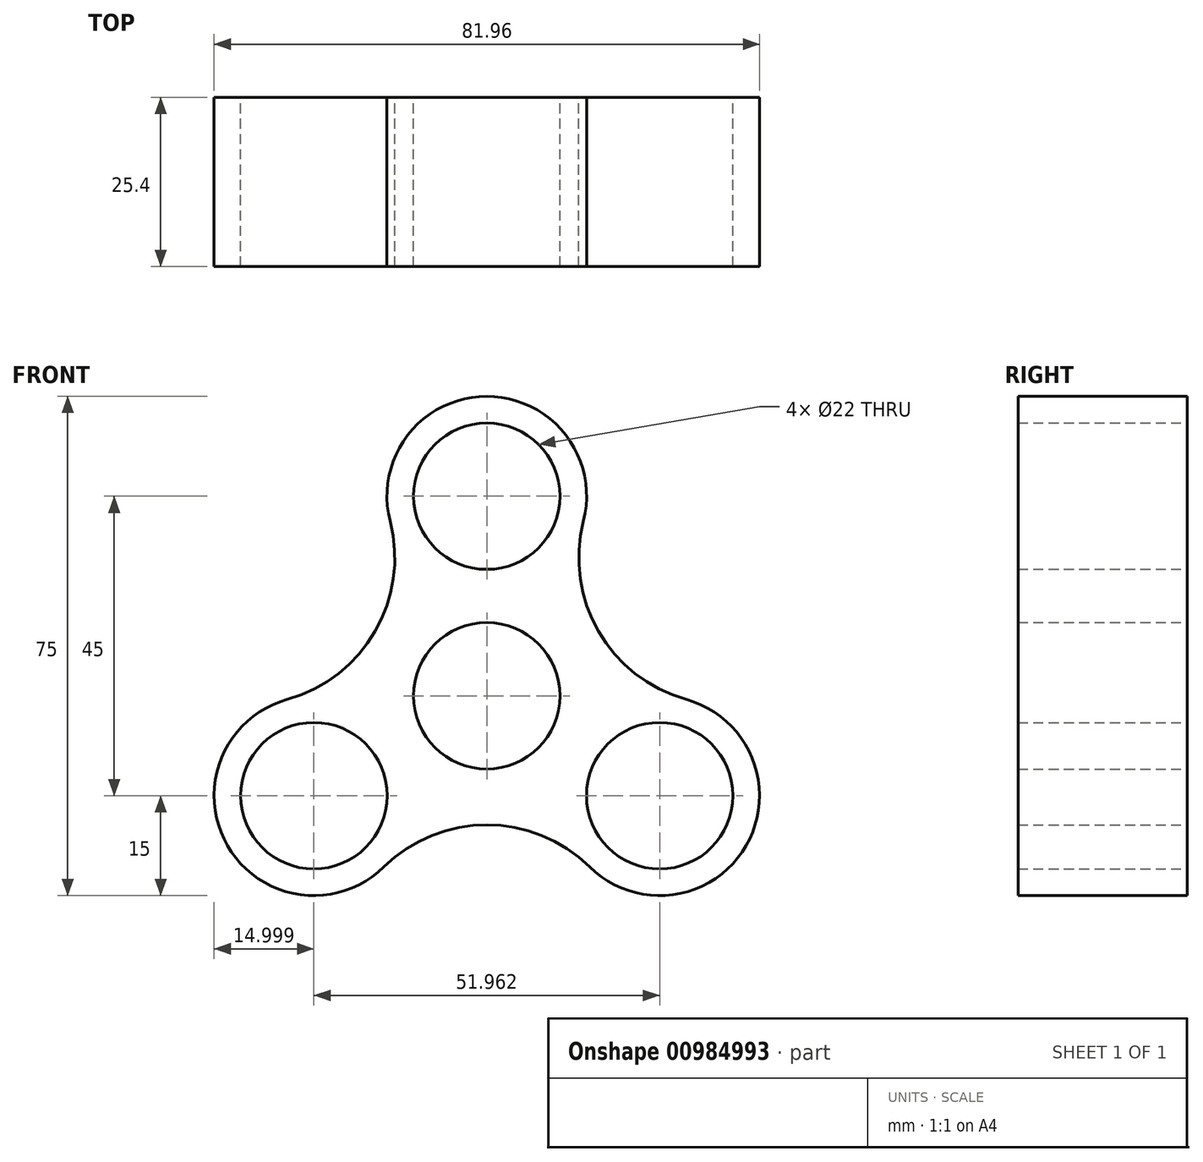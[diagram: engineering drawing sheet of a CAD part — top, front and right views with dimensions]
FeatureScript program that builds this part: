
annotation { "Feature Type Name" : "Feature", "Feature Type Description" : "" }
export const myFeature = defineFeature(function(context is Context, id is Id, definition is map)
    precondition{}
    {
        {
            var Q0;
            Q0=qCreatedBy(makeId("Front.planeOp"),FACE);
            var sketch = newSketch(context, id + "F0", { "sketchPlane" : qUnion([Q0])});
            skCircle(sketch, "E0.cCircle", {"center": v(0, 0) * mm, "radius": 30 * mm, "construction": true});
            skLineSegment(sketch, "E0.0", {"start": v(51.96, -30) * mm, "end": v(-51.96, -30) * mm, "construction": true});
            skLineSegment(sketch, "E0.1", {"start": v(-51.96, -30) * mm, "end": v(0, 60) * mm, "construction": true});
            skLineSegment(sketch, "E0.2", {"start": v(0, 60) * mm, "end": v(51.96, -30) * mm, "construction": true});
            skPoint(sketch, "E0.0.midPoint", {"position": v(0, -30) * mm});
            skArc(sketch, "E1", {"start": v(14.52, 26.25) * mm, "mid": v(0, 45) * mm, "end": v(-14.52, 26.25) * mm});
            skArc(sketch, "E2", {"start": v(15.47, -25.7) * mm, "mid": v(38.97, -22.5) * mm, "end": v(30, -0.55) * mm});
            skArc(sketch, "E3", {"start": v(-30, -0.55) * mm, "mid": v(-38.97, -22.5) * mm, "end": v(-15.47, -25.7) * mm});
            skCircle(sketch, "E4", {"center": v(0, 30) * mm, "radius": 11 * mm});
            skCircle(sketch, "E5", {"center": v(0, 0) * mm, "radius": 11 * mm});
            skCircle(sketch, "E6", {"center": v(25.98, -15) * mm, "radius": 11 * mm});
            skCircle(sketch, "E7", {"center": v(-25.98, -15) * mm, "radius": 11 * mm});
            skArc(sketch, "E8.2.0", {"start": v(14.52, 26.25) * mm, "mid": v(16.78, 9.69) * mm, "end": v(30, -0.55) * mm});
            skArc(sketch, "E9.1.0", {"start": v(-30, -0.55) * mm, "mid": v(-16.78, 9.69) * mm, "end": v(-14.52, 26.25) * mm});
            skArc(sketch, "E9.2.0", {"start": v(15.47, -25.7) * mm, "mid": v(0, -19.38) * mm, "end": v(-15.47, -25.7) * mm});
            skSolve(sketch);
        }
        {
            var Q0;
            Q0=makeQuery(id+"F0.imprint","IMPRINT",FACE,{"disambiguationData":[TD([[makeQuery(id+"F0.imprint","IMPRINT",EDGE,{"derivedFrom":sQuery(id+"F0.wireOp",EDGE,"E1")}),1.0]])]});
            extrude(context, id + "F1", {"entities" : qUnion([Q0]), "depth" : 25.4 * mm, "offsetDistance" : 25.4 * mm});
        }
    });
